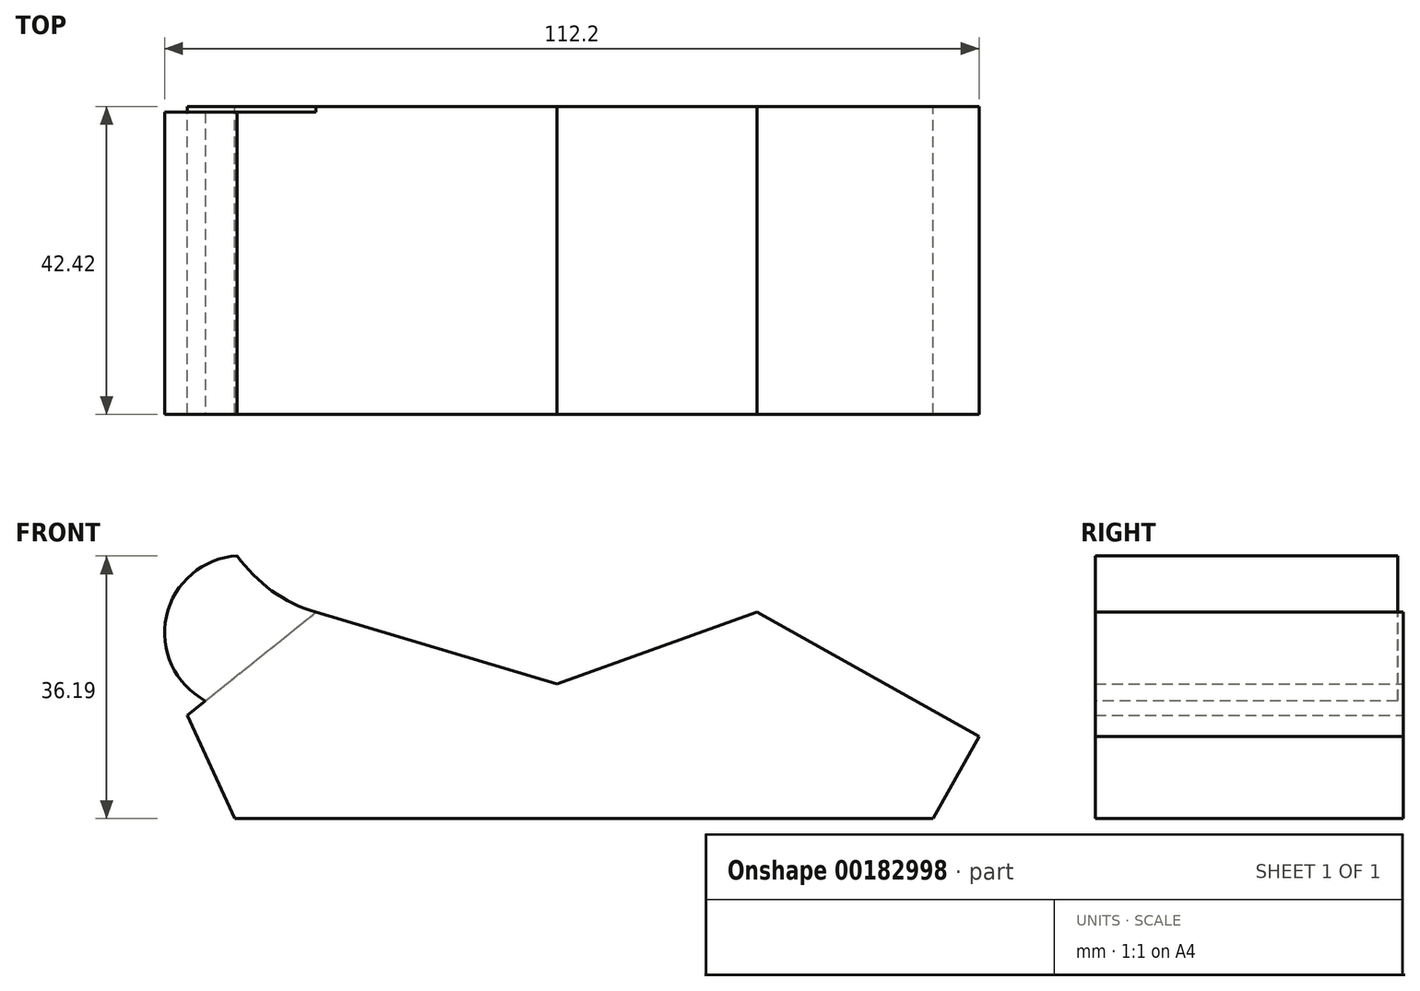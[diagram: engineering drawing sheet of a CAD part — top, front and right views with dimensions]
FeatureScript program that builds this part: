
annotation { "Feature Type Name" : "Feature", "Feature Type Description" : "" }
export const myFeature = defineFeature(function(context is Context, id is Id, definition is map)
    precondition{}
    {
        {
            var Q0;
            Q0=qCreatedBy(makeId("Front.planeOp"),FACE);
            var sketch = newSketch(context, id + "F0", { "sketchPlane" : qUnion([Q0])});
            skLineSegment(sketch, "E0.bottom", {"start": v(-50.93, 28.42) * mm, "end": v(58.16, 28.42) * mm});
            skLineSegment(sketch, "E0.top", {"start": v(-50.93, 0) * mm, "end": v(58.16, 0) * mm});
            skLineSegment(sketch, "E0.left", {"start": v(-50.93, 28.42) * mm, "end": v(-50.93, 0) * mm});
            skLineSegment(sketch, "E0.right", {"start": v(58.16, 28.42) * mm, "end": v(58.16, 0) * mm});
            skLineSegment(sketch, "E1", {"start": v(-33.19, 28.42) * mm, "end": v(0, 18.56) * mm});
            skLineSegment(sketch, "E2", {"start": v(0, 18.56) * mm, "end": v(27.6, 28.42) * mm});
            skLineSegment(sketch, "E3", {"start": v(27.6, 28.42) * mm, "end": v(58.16, 11.34) * mm});
            skLineSegment(sketch, "E4", {"start": v(58.16, 11.34) * mm, "end": v(51.82, 0) * mm});
            skLineSegment(sketch, "E5", {"start": v(51.82, 0) * mm, "end": v(-44.36, 0) * mm});
            skLineSegment(sketch, "E6", {"start": v(-44.36, 0) * mm, "end": v(-50.93, 14.21) * mm});
            skLineSegment(sketch, "E7", {"start": v(-50.93, 14.21) * mm, "end": v(-33.19, 28.42) * mm});
            skSolve(sketch);
        }
        {
            var Q0;
            Q0=makeQuery(id+"F0.imprint","IMPRINT",FACE,{"disambiguationData":[TD([[makeQuery(id+"F0.imprint","IMPRINT",EDGE,{"derivedFrom":sQuery(id+"F0.wireOp",EDGE,"E1")}),-1.0]])]});
            extrude(context, id + "F1", {"entities" : qUnion([Q0]), "depth" : 42.42 * mm});
        }
        {
            var Q0;
            Q0=makeQuery(id+"F1.opExtrude","CAP_FACE",FACE,{"disambiguationData":[OSD([sQuery(id+"F0.wireOp",EDGE,"E1"),sQuery(id+"F0.wireOp",EDGE,"E2"),sQuery(id+"F0.wireOp",EDGE,"E3"),sQuery(id+"F0.wireOp",EDGE,"E4"),sQuery(id+"F0.wireOp",EDGE,"E5"),sQuery(id+"F0.wireOp",EDGE,"E6"),sQuery(id+"F0.wireOp",EDGE,"E7")])],"isStart":false});
            var sketch = newSketch(context, id + "F2", { "sketchPlane" : qUnion([Q0])});
            skArc(sketch, "E8", {"start": v(-44.03, 36.2) * mm, "mid": v(-53.79, 27.87) * mm, "end": v(-48.41, 16.23) * mm});
            skArc(sketch, "E9", {"start": v(-44.03, 36.2) * mm, "mid": v(-39.26, 31.4) * mm, "end": v(-33.19, 28.42) * mm});
            skSolve(sketch);
        }
        {
            var Q0;
            Q0 = qSketchRegion(id + "F2", true);
            var Q1;
            {var subQ0=sQuery(id+"F2.wireOp",EDGE,"E8");Q1=makeQuery(id+"F2.imprint","IMPRINT",FACE,{"disambiguationData":[TD([[makeQuery(id+"F2.imprint","IMPRINT",EDGE,{"derivedFrom":subQ0}),1.0]])]});}
            extrude(context, id + "F3", {"entities" : qUnion([Q0, Q1]), "operationType" : NewBodyOperationType.ADD, "oppositeDirection" : true, "depth" : 42.67 * mm});
        }
        {
            var Q0;
            Q0=makeQuery(id+"F3.opExtrude","CAP_FACE",FACE,{"disambiguationData":[OSD([sQuery(id+"F0.wireOp",EDGE,"E7"),sQuery(id+"F2.wireOp",EDGE,"E8"),sQuery(id+"F2.wireOp",EDGE,"E9")])],"isStart":false});
            extrude(context, id + "F4", {"entities" : qUnion([Q0]), "operationType" : NewBodyOperationType.REMOVE, "oppositeDirection" : true, "depth" : 1.02 * mm});
        }
    });
